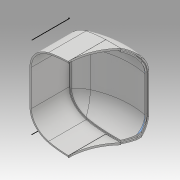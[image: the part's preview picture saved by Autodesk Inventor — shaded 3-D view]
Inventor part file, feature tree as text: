
AUTODESK INVENTOR PART (.ipt)
format: ipt  version: 2017 (Build 210142000, 142)  size: 914,432 bytes
history: native  units: mm
features: sketch x9, extrude x8, other x3, projected_geometry x2, shell x1, plane x1
ambient origin geometry x8: Origin, YZ Plane, XZ Plane, XY Plane, X Axis, Y Axis, Z Axis, Center Point
bodies: Solid1 (feature_tree)
feature tree (24):
  other  "Cabeza0.ipt"
  extrude  "Extrusion20"  TaperAngle=0.0deg  [1 undecoded]
  extrude  "Extrusion27"  Depth=5.0mm TaperAngle=0.0deg
  shell  "Shell4"  Thickness=1.0mm
  extrude  "Extrusion28"  Depth=30.0mm TaperAngle=0.0deg
  extrude  "Extrusion29"  Depth=300.0mm TaperAngle=0.0deg
  extrude  "Extrusion35"  Depth=67.0mm
  extrude  "Extrusion37"  [1 undecoded]
  extrude  "Extrusion38"  [1 undecoded]
  plane  "Work Plane3"
  sketch  "Sketch60"
  extrude  "Extrusion39"  [1 undecoded]
  other  "Solid1::Cabeza0.ipt"
  other  "TaggingFeature1"
  sketch  "Sketch35"  dims[d0=13.0mm d76=0.0mm d78=0.0mm]
  sketch  "Sketch47"  dims[d85=190.0mm d86=0.0mm d118=5.0mm d119=0.0mm d120=1.0mm]
  sketch  "Sketch48"  dims[d123=150.0mm d124=0.0mm d125=30.0mm d126=0.0mm]
  sketch  "Sketch49"  dims[d138=80.0mm d139=0.0mm d142=300.0mm d143=0.0mm]
  projected_geometry  "Projected Loop31"
  sketch  "Sketch55"  dims[d144=1.5mm d145=0.0mm d146=67.0mm]
  sketch  "Sketch57"  dims[d147=1.5mm d148=0.0mm]
  sketch  "Sketch58"
  projected_geometry  "Projected Loop34"
  sketch  "Sketch61"
note: 4 required parameter values undecoded (feature->parameter linkage not recoverable at this tier; creation-order binding heuristic only, values carry confidence <= 0.55)
